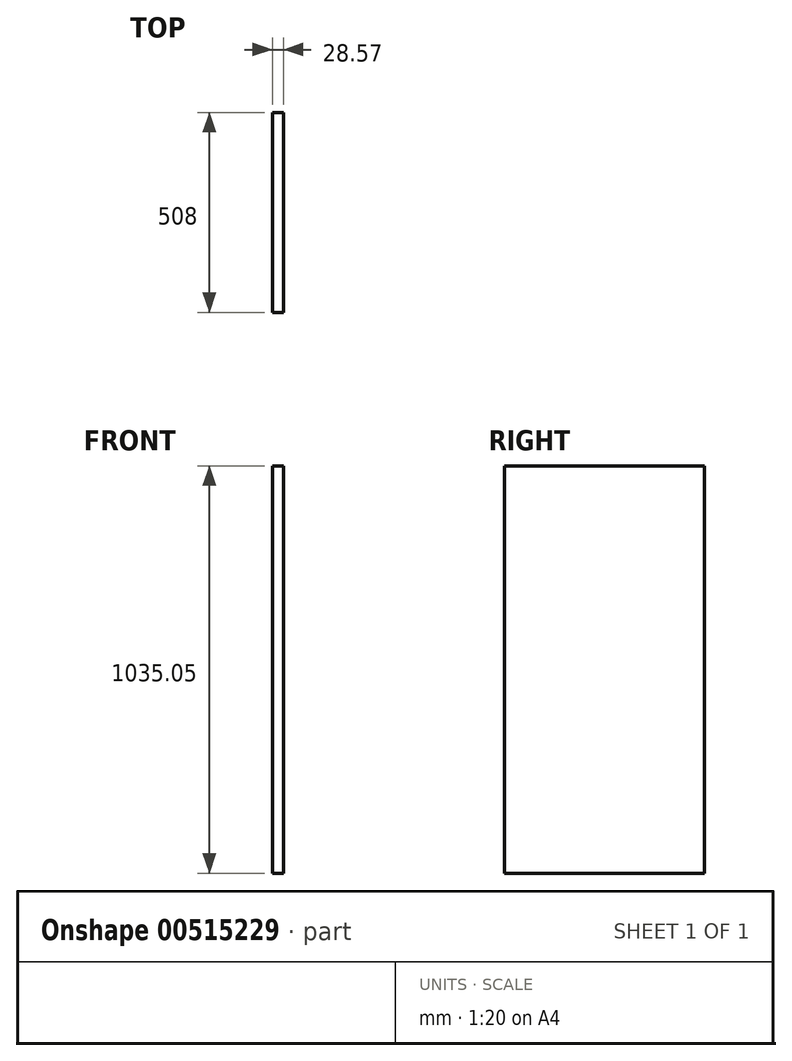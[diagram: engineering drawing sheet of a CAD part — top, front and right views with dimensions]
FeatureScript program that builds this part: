
annotation { "Feature Type Name" : "Feature", "Feature Type Description" : "" }
export const myFeature = defineFeature(function(context is Context, id is Id, definition is map)
    precondition{}
    {
        {
            var Q0;
            Q0=qCreatedBy(makeId("Right.planeOp"),FACE);
            var sketch = newSketch(context, id + "F0", { "sketchPlane" : qUnion([Q0])});
            skLineSegment(sketch, "E0.bottom", {"start": v(254, 352.43) * mm, "end": v(-254, 352.43) * mm});
            skLineSegment(sketch, "E0.top", {"start": v(254, -352.43) * mm, "end": v(-254, -352.43) * mm});
            skLineSegment(sketch, "E0.left", {"start": v(254, 352.43) * mm, "end": v(254, -352.43) * mm});
            skLineSegment(sketch, "E0.right", {"start": v(-254, 352.43) * mm, "end": v(-254, -352.43) * mm});
            skPoint(sketch, "E0.middle", {"position": v(0, 0) * mm});
            skSolve(sketch);
        }
        {
            var Q0;
            Q0=makeQuery(id+"F0.imprint","IMPRINT",FACE,{"disambiguationData":[TD([[makeQuery(id+"F0.imprint","IMPRINT",EDGE,{"derivedFrom":sQuery(id+"F0.wireOp",EDGE,"E0.bottom")}),1.0]])]});
            extrude(context, id + "F1", {"entities" : qUnion([Q0]), "depth" : 28.57 * mm});
        }
        {
            var Q0;
            Q0=makeQuery(id+"F1.opExtrude","SWEPT_FACE",FACE,{"disambiguationData":[OSD([sQuery(id+"F0.wireOp",EDGE,"E0.bottom")])]});
            extrude(context, id + "F2", {"entities" : qUnion([Q0]), "operationType" : NewBodyOperationType.ADD, "depth" : 330.2 * mm});
        }
    });
